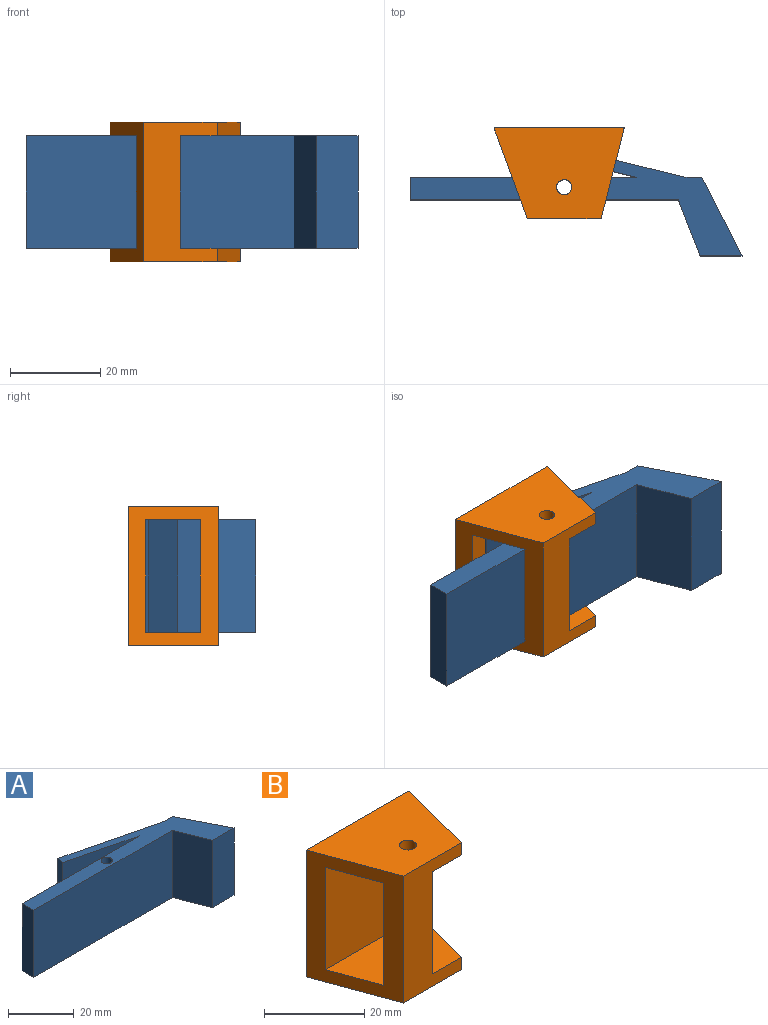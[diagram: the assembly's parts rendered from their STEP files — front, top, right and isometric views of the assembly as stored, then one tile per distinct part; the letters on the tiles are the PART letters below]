
ASSEMBLY  parts=2 mates=1
PART A: 13 faces, bbox 73.7x26.5x25 mm
  f0: plane 50.35x25mm, normal (0,1,0), area 1258.8mm2, adj f1,f9,f10,f11
  f1: plane 25x5mm, normal (-1,0,0), area 125mm2, adj f0,f2,f10,f11
  f2: plane 59.56x25mm, normal (0,-1,0), area 1489.1mm2, adj f1,f3,f10,f11
  f3: plane 25x12.41mm, normal (-0.93,-0.36,0), area 333.1mm2, adj f2,f4,f10,f11
  f4: plane 25x9.31mm, normal (0,-1,0), area 232.7mm2, adj f3,f5,f10,f11
  f5: plane 25x17.41mm, normal (0.89,0.45,0), area 488.8mm2, adj f4,f6,f10,f11
  f6: plane 25x3.55mm, normal (0,1,0), area 88.7mm2, adj f5,f7,f10,f11
  f7: plane 36.75x25mm, normal (0.24,0.97,0), area 946.3mm2, adj f6,f8,f10,f11
  f8: plane 25x2.55mm, normal (-0.97,0.24,0), area 65.5mm2, adj f7,f9,f10,f11
  f9: plane 26.45x25mm, normal (-0.24,-0.97,0), area 681.1mm2, adj f0,f8,f10,f11
  f10: plane 73.72x26.49mm, normal (0,0,1), area 513mm2, adj f0,f1,f2,f3,f4,f5,f6,f7
  f11: plane 73.72x26.49mm, normal (0,0,-1), area 513mm2, adj f0,f1,f2,f3,f4,f5,f6,f7
  f12: cylinder r=1.7mm len=25mm, axis (0,0,-1), area 267mm2, adj f10,f11
PART B: 13 faces, bbox 28.9x20.1x31 mm
  f0: plane 26.46x16.23mm, normal (0,0,-1), area 301.2mm2, adj f1,f2,f3,f6,f7,f8,f11
  f1: plane 31x20.14mm, normal (-0.94,-0.34,0), area 344.7mm2, adj f0,f2,f4,f5,f6,f8,f9,f10
  f2: plane 31x16.4mm, normal (0,-1,0), area 303.4mm2, adj f0,f1,f3,f5,f7,f9,f10
  f3: plane 31x20.14mm, normal (0.97,-0.25,0), area 225.5mm2, adj f0,f2,f4,f5,f6,f9,f10
  f4: plane 31x28.89mm, normal (0,1,0), area 895.4mm2, adj f1,f3,f5,f10
  f5: plane 28.89x20.14mm, normal (0,0,1), area 447mm2, adj f1,f2,f3,f4,f11
  f6: plane 26.46x25mm, normal (0,-1,0), area 661.6mm2, adj f0,f1,f3,f9
  f7: plane 25x4.2mm, normal (1,0,0), area 105.1mm2, adj f0,f2,f8,f9
  f8: plane 25x9.74mm, normal (0,1,0), area 243.5mm2, adj f0,f1,f7,f9
  f9: plane 26.46x16.23mm, normal (0,0,1), area 301.2mm2, adj f1,f2,f3,f6,f7,f8,f12
  f10: plane 28.89x20.14mm, normal (0,0,-1), area 447mm2, adj f1,f2,f3,f4,f12
  f11: cylinder r=1.7mm len=3.4mm, axis (0,0,-1), area 32mm2, adj f0,f5
  f12: cylinder r=1.7mm len=3.4mm, axis (0,0,1), area 32mm2, adj f9,f10
PLACE A t=(9.33,-31.2,1.4)mm
PLACE B t=(9.33,-31.2,1.4)mm fixed
MATE revolute A.f12 <-> B.f11  axis (0,0,-1) through (-0.06,9.8,1.4)mm
